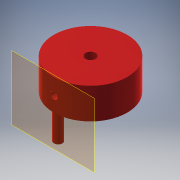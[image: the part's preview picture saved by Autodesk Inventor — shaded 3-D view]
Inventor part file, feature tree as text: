
AUTODESK INVENTOR PART (.ipt)
format: ipt  version: 2016 (Build 200138000, 138)  size: 130,048 bytes
history: native  units: mm
features: reference x6, sketch x4, plane x4, extrude x3, thicken_offset x2, hole x1
ambient origin geometry x8: Origin, YZ Plane, XZ Plane, XY Plane, X Axis, Y Axis, Z Axis, Center Point
bodies: Solid1 (feature_tree)
feature tree (20):
  sketch  "Sketch1"  dims[d0=10.0mm d1=0.0mm d2=10.0mm d3=0.0mm]
  plane  "Work Plane1"
  extrude  "Extrusion1"  Depth=10.0mm TaperAngle=0.0deg
  sketch  "Sketch2"  dims[d4=15.0mm d5=0.0mm]
  plane  "Work Plane2"
  extrude  "Extrusion2"  TaperAngle=0.0deg  [1 undecoded]
  extrude  "Extrusion3"  Depth=2.0mm
  plane  "Work Plane4"
  hole  "Hole1"  [1 undecoded]
  thicken_offset  "Thicken1"
  thicken_offset  "Thicken2"
  reference  "Reference1"
  reference  "Reference2"
  reference  "Reference3"
  reference  "Reference4"
  reference  "Reference5"
  reference  "Reference6"
  sketch  "Sketch3"  dims[d6=0.6mm d7=0.6mm]
  plane  "Work Plane3"
  sketch  "Sketch4"  dims[d8=4.0mm d9=6.0mm d10=4.0mm d11=2.0mm d12=90.0deg d13=8.0mm d14=20.594885mm d15=0.4mm d16=0.4mm]
note: 2 required parameter values undecoded (feature->parameter linkage not recoverable at this tier; creation-order binding heuristic only, values carry confidence <= 0.55)
